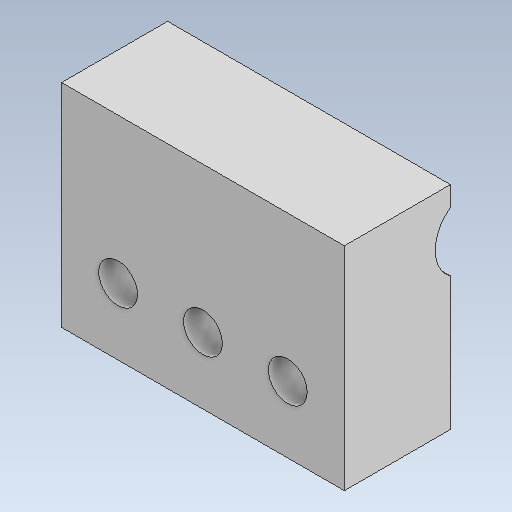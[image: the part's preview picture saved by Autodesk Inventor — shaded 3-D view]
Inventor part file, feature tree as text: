
AUTODESK INVENTOR PART (.ipt)
format: ipt  version: 2020 (Build 240168000, 168)  size: 123,392 bytes
history: native  units: mm
features: sketch x3, extrude x2, hole x1
ambient origin geometry x8: Origin, YZ Plane, XZ Plane, XY Plane, X Axis, Y Axis, Z Axis, Center Point
bodies: Solid1 (feature_tree)
feature tree (6):
  extrude  "Extrusion1"  Depth=40.0mm
  extrude  "Extrusion2"  Depth=15.0mm
  hole  "Hole1"  [1 undecoded]
  sketch  "Sketch1"  dims[d0=30.0mm d1=40.0mm]
  sketch  "Sketch2"  dims[d2=15.0mm d3=0.0mm d5=10.3mm]
  sketch  "Sketch3"  dims[d6=0.0mm d7=0.0mm d9=5.5mm d10=6.0mm d11=4.0mm d12=2.0mm d13=90.0deg d14=8.0mm d15=20.594885mm d17=23.0mm d18=3.0mm d19=8.0mm d20=8.0mm]
note: 1 required parameter value undecoded (feature->parameter linkage not recoverable at this tier; creation-order binding heuristic only, values carry confidence <= 0.55)
